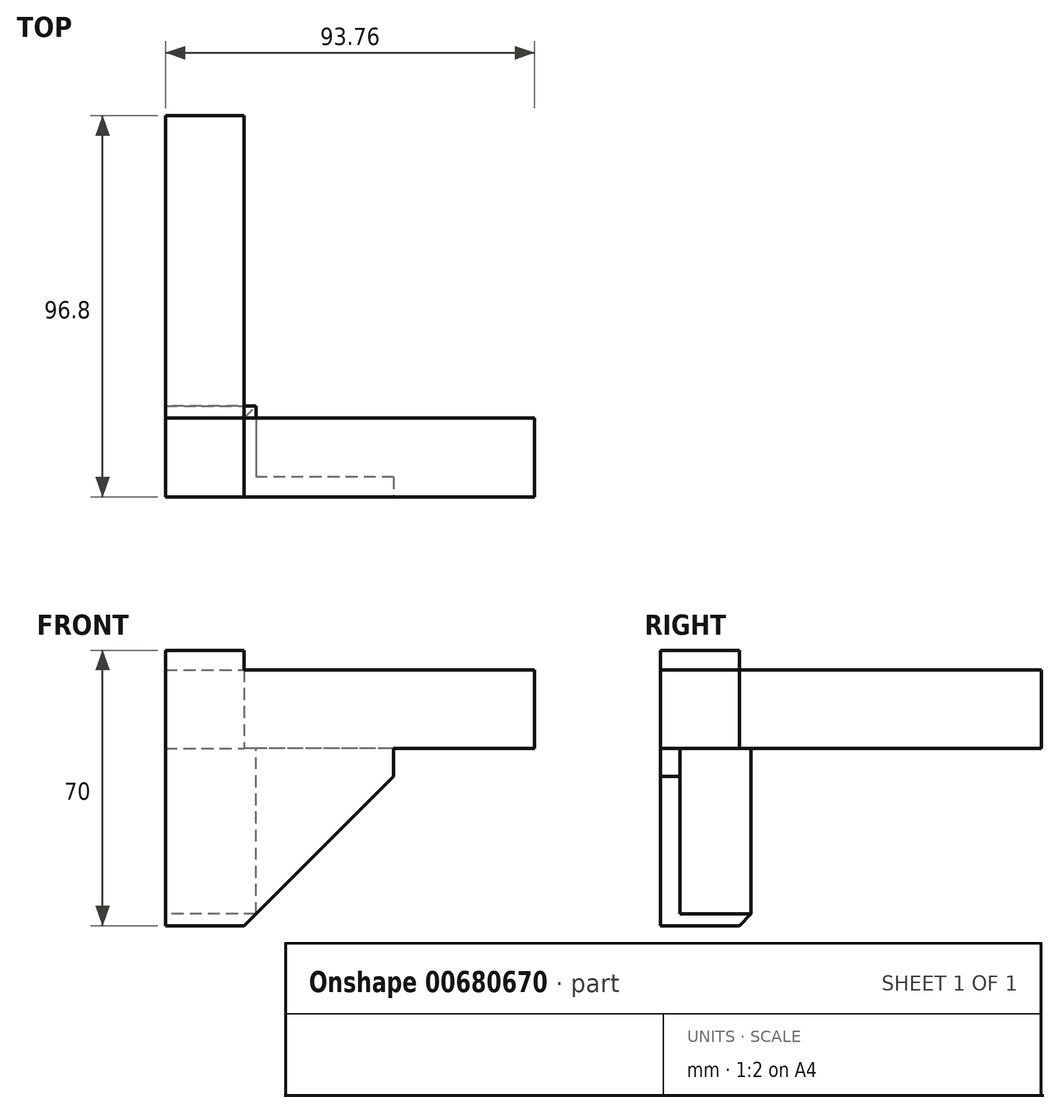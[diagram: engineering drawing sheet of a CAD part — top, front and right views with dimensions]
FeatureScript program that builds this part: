
annotation { "Feature Type Name" : "Feature", "Feature Type Description" : "" }
export const myFeature = defineFeature(function(context is Context, id is Id, definition is map)
    precondition{}
    {
        {
            var Q0;
            Q0=qCreatedBy(makeId("Top.planeOp"),FACE);
            var sketch = newSketch(context, id + "F0", { "sketchPlane" : qUnion([Q0])});
            skLineSegment(sketch, "E0.bottom", {"start": v(-20, 76.8) * mm, "end": v(0, 76.8) * mm});
            skLineSegment(sketch, "E0.top", {"start": v(-20, 0) * mm, "end": v(0, 0) * mm});
            skLineSegment(sketch, "E0.left", {"start": v(-20, 76.8) * mm, "end": v(-20, 0) * mm});
            skLineSegment(sketch, "E0.right", {"start": v(0, 76.8) * mm, "end": v(0, 0) * mm});
            skLineSegment(sketch, "E1.bottom", {"start": v(73.76, -20) * mm, "end": v(0, -20) * mm});
            skLineSegment(sketch, "E1.top", {"start": v(73.76, 0) * mm, "end": v(0, 0) * mm});
            skLineSegment(sketch, "E1.left", {"start": v(73.76, -20) * mm, "end": v(73.76, 0) * mm});
            skLineSegment(sketch, "E1.right", {"start": v(0, -20) * mm, "end": v(0, 0) * mm});
            skLineSegment(sketch, "E2.top", {"start": v(-20, -20) * mm, "end": v(0, -20) * mm});
            skLineSegment(sketch, "E2.left", {"start": v(-20, 0) * mm, "end": v(-20, -20) * mm});
            skLineSegment(sketch, "E2.right", {"start": v(0, 0) * mm, "end": v(0, -20) * mm});
            skSolve(sketch);
        }
        {
            var Q0;
            Q0=makeQuery(id+"F0.imprint","IMPRINT",FACE,{"disambiguationData":[TD([[makeQuery(id+"F0.imprint","IMPRINT",EDGE,{"derivedFrom":sQuery(id+"F0.wireOp",EDGE,"E0.bottom")}),-1.0]])]});
            var Q1;
            Q1=makeQuery(id+"F0.imprint","IMPRINT",FACE,{"disambiguationData":[TD([[makeQuery(id+"F0.imprint","IMPRINT",EDGE,{"derivedFrom":sQuery(id+"F0.wireOp",EDGE,"E1.bottom")}),-1.0]])]});
            extrude(context, id + "F1", {"entities" : qUnion([Q0, Q1]), "depth" : 20 * mm, "offsetDistance" : 25 * mm});
        }
        {
            var Q0;
            Q0=makeQuery(id+"F0.imprint","IMPRINT",FACE,{"disambiguationData":[TD([[makeQuery(id+"F0.imprint","IMPRINT",EDGE,{"derivedFrom":sQuery(id+"F0.wireOp",EDGE,"E0.top")}),-1.0]])]});
            extrude(context, id + "F2", {"entities" : qUnion([Q0]), "oppositeDirection" : true, "depth" : 25 * mm, "offsetDistance" : 25 * mm, "hasSecondDirection" : true, "secondDirectionOppositeDirection" : false, "secondDirectionDepth" : 25 * mm});
        }
        {
            var Q0;
            Q0=makeQuery(id+"F2.opExtrude","SWEPT_FACE",FACE,{"disambiguationData":[OSD([sQuery(id+"F0.wireOp",EDGE,"E2.left")])]});
            var sketch = newSketch(context, id + "F3", { "sketchPlane" : qUnion([Q0])});
            skLineSegment(sketch, "E3", {"start": v(20, -25) * mm, "end": v(20, -45) * mm});
            skLineSegment(sketch, "E4", {"start": v(20, -45) * mm, "end": v(0, -45) * mm});
            skLineSegment(sketch, "E5", {"start": v(0, -45) * mm, "end": v(0, -25) * mm});
            skLineSegment(sketch, "E6", {"start": v(0, -25) * mm, "end": v(20, -25) * mm});
            skLineSegment(sketch, "E7", {"start": v(0, -45) * mm, "end": v(-38, -7) * mm});
            skLineSegment(sketch, "E8", {"start": v(-38, -7) * mm, "end": v(-38, 0) * mm});
            skLineSegment(sketch, "E9", {"start": v(-38, 0) * mm, "end": v(0, 0) * mm});
            skLineSegment(sketch, "E10", {"start": v(0, 0) * mm, "end": v(0, -25) * mm});
            skSolve(sketch);
        }
        {
            var Q0;
            Q0=makeQuery(id+"F3.imprint","IMPRINT",FACE,{"disambiguationData":[TD([[makeQuery(id+"F3.imprint","IMPRINT",EDGE,{"derivedFrom":sQuery(id+"F3.wireOp",EDGE,"E3")}),-1.0]])]});
            extrude(context, id + "F4", {"entities" : qUnion([Q0]), "oppositeDirection" : true, "depth" : 20 * mm, "offsetDistance" : 25 * mm});
        }
        {
            var Q0;
            Q0=makeQuery(id+"F3.imprint","IMPRINT",FACE,{"disambiguationData":[TD([[makeQuery(id+"F3.imprint","IMPRINT",EDGE,{"derivedFrom":sQuery(id+"F3.wireOp",EDGE,"E5")}),1.0]])]});
            extrude(context, id + "F5", {"entities" : qUnion([Q0]), "operationType" : NewBodyOperationType.ADD, "oppositeDirection" : true, "depth" : 5 * mm, "offsetDistance" : 25 * mm});
        }
        {
            var Q0;
            Q0=makeQuery(id+"F4.opExtrude","SWEPT_FACE",FACE,{"disambiguationData":[OSD([sQuery(id+"F3.wireOp",EDGE,"E3")])]});
            var sketch = newSketch(context, id + "F6", { "sketchPlane" : qUnion([Q0])});
            skLineSegment(sketch, "E11", {"start": v(0, -45) * mm, "end": v(38, -7) * mm});
            skLineSegment(sketch, "E12", {"start": v(38, -7) * mm, "end": v(38, 0) * mm});
            skLineSegment(sketch, "E13", {"start": v(38, 0) * mm, "end": v(0, 0) * mm});
            skLineSegment(sketch, "E14", {"start": v(0, 0) * mm, "end": v(0, -45) * mm});
            skSolve(sketch);
        }
        {
            var Q0;
            {var subQ4=sQuery(id+"F6.wireOp",EDGE,"E11");Q0=makeQuery(id+"F6.imprint","IMPRINT",FACE,{"disambiguationData":[TD([[makeQuery(id+"F6.imprint","IMPRINT",EDGE,{"derivedFrom":subQ4}),1.0]])]});}
            extrude(context, id + "F7", {"entities" : qUnion([Q0]), "operationType" : NewBodyOperationType.ADD, "oppositeDirection" : true, "depth" : 5 * mm, "offsetDistance" : 25 * mm});
        }
        {
            var Q0;
            Q0=qCreatedBy(makeId("Top.planeOp"),FACE);
            var sketch = newSketch(context, id + "F8", { "sketchPlane" : qUnion([Q0])});
            skLineSegment(sketch, "E15", {"start": v(-15, 3) * mm, "end": v(3, 3) * mm});
            skLineSegment(sketch, "E16", {"start": v(3, 3) * mm, "end": v(3, -15) * mm});
            skLineSegment(sketch, "E17", {"start": v(3, -15) * mm, "end": v(0, -15) * mm});
            skLineSegment(sketch, "E18", {"start": v(0, -15) * mm, "end": v(0, 0) * mm});
            skLineSegment(sketch, "E19", {"start": v(0, 0) * mm, "end": v(-15, 0) * mm});
            skLineSegment(sketch, "E20", {"start": v(-15, 0) * mm, "end": v(-15, 3) * mm});
            skSolve(sketch);
        }
        {
            var Q0;
            Q0=makeQuery(id+"F8.imprint","IMPRINT",FACE,{"disambiguationData":[TD([[makeQuery(id+"F8.imprint","IMPRINT",EDGE,{"derivedFrom":sQuery(id+"F8.wireOp",EDGE,"E15")}),-1.0]])]});
            extrude(context, id + "F9", {"entities" : qUnion([Q0]), "operationType" : NewBodyOperationType.ADD, "oppositeDirection" : true, "depth" : 45 * mm, "offsetDistance" : 25 * mm});
        }
        {
            var Q0;
            Q0=makeQuery(id+"F9.opExtrude","SWEPT_FACE",FACE,{"disambiguationData":[OSD([sQuery(id+"F8.wireOp",EDGE,"E20")])]});
            extrude(context, id + "F10", {"entities" : qUnion([Q0]), "operationType" : NewBodyOperationType.REMOVE, "oppositeDirection" : true, "depth" : 25 * mm, "offsetDistance" : 25 * mm});
        }
        {
            var Q0;
            Q0=makeQuery(id+"F9.opExtrude","SWEPT_FACE",FACE,{"disambiguationData":[OSD([sQuery(id+"F8.wireOp",EDGE,"E17")])]});
            extrude(context, id + "F11", {"entities" : qUnion([Q0]), "operationType" : NewBodyOperationType.REMOVE, "oppositeDirection" : true, "depth" : 25 * mm, "offsetDistance" : 25 * mm});
        }
        {
            var Q0;
            Q0=makeQuery(id+"F5.opExtrude","CAP_FACE",FACE,{"disambiguationData":[OSD([sQuery(id+"F3.wireOp",EDGE,"E5"),sQuery(id+"F3.wireOp",EDGE,"E7"),sQuery(id+"F3.wireOp",EDGE,"E8"),sQuery(id+"F3.wireOp",EDGE,"E9"),sQuery(id+"F3.wireOp",EDGE,"E10")])],"isStart":false});
            extrude(context, id + "F12", {"entities" : qUnion([Q0]), "operationType" : NewBodyOperationType.REMOVE, "oppositeDirection" : true, "depth" : 25 * mm, "offsetDistance" : 25 * mm});
        }
    });
